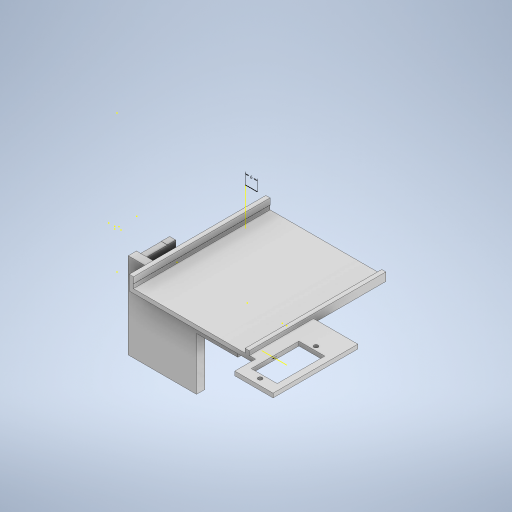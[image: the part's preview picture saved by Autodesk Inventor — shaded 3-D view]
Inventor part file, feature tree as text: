
AUTODESK INVENTOR PART (.ipt)
format: ipt  version: 2023 (Build 270158000, 158)  size: 867,840 bytes
history: native  units: mm
features: sketch x88, extrude x69, thread x4
ambient origin geometry x8: Origin, YZ Plane, XZ Plane, XY Plane, X Axis, Y Axis, Z Axis, Center Point
bodies: Solid1 (feature_tree)
feature tree (161):
  extrude  "Extrusion1"  Depth=50.0mm
  sketch  "Sketch2"  dims[d2=2.0mm d3=0.0mm d4=4.0mm]
  extrude  "Extrusion2"  Depth=4.0mm
  sketch  "Sketch4"  dims[d9=2.0mm d10=17.5mm d11=0.0mm]
  extrude  "Extrusion3"  Depth=1.0mm TaperAngle=0.0deg
  extrude  "Extrusion4"  Depth=17.5mm TaperAngle=0.0deg
  extrude  "Extrusion5"  Depth=2.0mm
  extrude  "Extrusion6"  Depth=2.0mm
  extrude  "Extrusion7"  Depth=9.0mm
  sketch  "Sketch9"  dims[d25=20.5mm d26=0.0mm d27=2.0mm]
  extrude  "Extrusion8"  Depth=2.0mm TaperAngle=0.0deg
  extrude  "Extrusion9"  Depth=2.0mm
  extrude  "Extrusion10"  Depth=10.0mm TaperAngle=0.0deg
  extrude  "Extrusion11"  Depth=10.0mm TaperAngle=0.0deg
  extrude  "Extrusion12"  Depth=2.0mm
  extrude  "Extrusion13"  Depth=2.0mm TaperAngle=0.0deg
  extrude  "Extrusion14"  Depth=15.0mm
  extrude  "Extrusion15"  Depth=5.0mm TaperAngle=0.0deg
  extrude  "Extrusion16"  Depth=2.0mm
  extrude  "Extrusion17"  Depth=2.0mm
  sketch  "Sketch20"  dims[d65=5.0mm d66=0.0mm d67=2.0mm d68=0.0mm]
  extrude  "Extrusion18"  Depth=10.0mm TaperAngle=0.0deg
  extrude  "Extrusion19"  Depth=2.0mm
  sketch  "Sketch23"  dims[d77=2.0mm d78=2.0mm d79=0.0mm]
  sketch  "Sketch24"  dims[d80=18.0mm d81=2.0mm d82=0.0mm]
  extrude  "Extrusion20"  Depth=2.0mm TaperAngle=0.0deg
  extrude  "Extrusion21"  Depth=30.0mm TaperAngle=0.0deg
  extrude  "Extrusion22"  Depth=4.0mm TaperAngle=0.0deg
  sketch  "Sketch28"  dims[d96=2.0mm d97=10.0mm d98=0.0mm]
  extrude  "Extrusion23"  Depth=2.0mm TaperAngle=0.0deg
  extrude  "Extrusion24"  Depth=2.0mm TaperAngle=0.0deg
  sketch  "Sketch31"  dims[d107=6.0mm d108=0.0mm d109=3.0mm]
  extrude  "Extrusion25"  Depth=2.0mm
  extrude  "Extrusion26"  Depth=2.0mm
  thread  "Thread1"  [1 undecoded]
  thread  "Thread2"  [1 undecoded]
  extrude  "Extrusion27"  Depth=2.0mm TaperAngle=0.0deg
  extrude  "Extrusion28"  Depth=10.0mm TaperAngle=0.0deg
  extrude  "Extrusion29"  Depth=10.0mm TaperAngle=0.0deg
  extrude  "Extrusion30"  Depth=3.0mm TaperAngle=0.0deg
  extrude  "Extrusion31"  Depth=3.0mm
  extrude  "Extrusion32"  Depth=12.0mm TaperAngle=0.0deg
  extrude  "Extrusion33"  Depth=50.0mm TaperAngle=0.0deg
  sketch  "Sketch41"  dims[d141=10.0mm d142=0.0mm d143=20.0mm d144=0.0mm]
  sketch  "Sketch42"  dims[d145=2.0mm d146=2.0mm d147=0.0mm]
  extrude  "Extrusion34"  Depth=10.0mm TaperAngle=0.0deg
  extrude  "Extrusion35"  Depth=4.0mm TaperAngle=0.0deg
  sketch  "Sketch45"  dims[d156=3.0mm d157=10.0mm d158=0.0mm]
  extrude  "Extrusion36"  Depth=4.0mm
  sketch  "Sketch47"  dims[d162=3.0mm d163=26.0mm d164=0.0mm]
  extrude  "Extrusion37"  Depth=4.0mm
  extrude  "Extrusion38"  Depth=10.0mm TaperAngle=0.0deg
  extrude  "Extrusion39"  Depth=20.0mm TaperAngle=0.0deg
  extrude  "Extrusion40"  Depth=10.0mm TaperAngle=0.0deg
  extrude  "Extrusion41"  Depth=20.0mm TaperAngle=0.0deg
  sketch  "Sketch52"  dims[d178=10.0mm d179=0.0mm]
  extrude  "Extrusion42"  Depth=2.0mm TaperAngle=0.0deg
  sketch  "Sketch54"
  extrude  "Extrusion43"  Depth=3.0mm TaperAngle=0.0deg
  extrude  "Extrusion44"  Depth=5.0mm TaperAngle=0.0deg
  sketch  "Sketch57"
  sketch  "Sketch58"
  sketch  "Sketch59"
  extrude  "Extrusion45"  Depth=10.0mm TaperAngle=0.0deg
  extrude  "Extrusion46"  Depth=15.5mm TaperAngle=0.0deg
  sketch  "Sketch61"
  extrude  "Extrusion47"  Depth=3.0mm TaperAngle=0.0deg
  extrude  "Extrusion48"  Depth=3.0mm TaperAngle=0.0deg
  extrude  "Extrusion49"  Depth=2.0mm
  sketch  "Sketch65"
  extrude  "Extrusion50"  Depth=10.0mm TaperAngle=0.0deg
  extrude  "Extrusion51"  Depth=2.0mm TaperAngle=0.0deg
  extrude  "Extrusion52"  [1 undecoded]
  extrude  "Extrusion53"  [1 undecoded]
  extrude  "Extrusion54"  [1 undecoded]
  extrude  "Extrusion55"  [1 undecoded]
  extrude  "Extrusion56"  [1 undecoded]
  sketch  "Sketch73"
  extrude  "Extrusion57"  [1 undecoded]
  extrude  "Extrusion58"  [1 undecoded]
  sketch  "Sketch76"
  extrude  "Extrusion59"  [1 undecoded]
  extrude  "Extrusion60"  [1 undecoded]
  extrude  "Extrusion61"  [1 undecoded]
  extrude  "Extrusion62"  [1 undecoded]
  sketch  "Sketch81"
  extrude  "Extrusion63"  [1 undecoded]
  extrude  "Extrusion64"  [1 undecoded]
  extrude  "Extrusion65"  [1 undecoded]
  extrude  "Extrusion66"  [1 undecoded]
  extrude  "Extrusion67"  [1 undecoded]
  extrude  "Extrusion68"  [1 undecoded]
  thread  "Thread3"  [1 undecoded]
  thread  "Thread4"  [1 undecoded]
  extrude  "Extrusion69"  [1 undecoded]
  sketch  "Sketch1"  dims[d0=23.0mm d1=50.0mm]
  sketch  "Sketch3"  dims[d5=1.0mm d6=0.0mm d7=29.0mm d8=0.0mm]
  sketch  "Sketch5"  dims[d12=17.5mm d13=0.0mm d14=2.0mm]
  sketch  "Sketch6"  dims[d15=32.0mm d16=0.0mm d17=2.0mm]
  sketch  "Sketch7"  dims[d18=32.0mm d19=0.0mm d20=9.0mm]
  sketch  "Sketch8"  dims[d21=50.0mm d22=0.0mm d23=2.0mm d24=0.0mm]
  sketch  "Sketch10"  dims[d28=20.5mm d29=0.0mm d30=10.0mm d31=0.0mm]
  sketch  "Sketch11"  dims[d32=10.0mm d33=0.0mm d34=10.0mm d35=0.0mm]
  sketch  "Sketch12"  dims[d36=10.0mm d37=0.0mm d38=2.0mm]
  sketch  "Sketch13"  dims[d39=13.0mm d40=0.0mm d41=2.0mm d42=0.0mm]
  sketch  "Sketch14"  dims[d43=2.0mm d44=0.0mm d45=15.0mm]
  sketch  "Sketch15"  dims[d46=4.0mm d47=0.0mm d48=5.0mm d49=0.0mm]
  sketch  "Sketch16"  dims[d50=14.0mm d51=0.0mm d52=2.0mm]
  sketch  "Sketch17"  dims[d53=25.0mm d54=0.0mm d55=2.0mm]
  sketch  "Sketch18"  dims[d56=25.0mm d57=0.0mm d58=10.0mm d59=0.0mm]
  sketch  "Sketch19"  dims[d60=2.0mm d61=0.0mm d63=2.0mm]
  sketch  "Sketch21"  dims[d69=2.0mm d70=0.0mm d71=30.0mm d72=0.0mm]
  sketch  "Sketch22"  dims[d73=2.0mm d74=0.0mm d75=4.0mm d76=0.0mm]
  sketch  "Sketch25"  dims[d83=2.0mm d84=0.0mm d85=0.389mm]
  sketch  "Sketch26"  dims[d86=2.0mm d87=0.0mm d88=6.0mm d89=6.0mm d90=0.0mm d91=6.0mm d92=0.0mm]
  sketch  "Sketch27"  dims[d93=2.0mm d94=6.0mm d95=0.0mm]
  sketch  "Sketch29"  dims[d99=10.0mm d100=0.0mm d101=10.0mm d102=0.0mm]
  sketch  "Sketch30"  dims[d103=10.0mm d104=0.0mm d105=3.0mm d106=0.0mm]
  sketch  "Sketch32"  dims[d110=3.0mm d111=12.0mm d112=0.0mm]
  sketch  "Sketch33"  dims[d113=60.0mm d114=0.0mm d115=50.0mm d116=0.0mm]
  sketch  "Sketch34"  dims[d117=50.0mm d118=0.0mm d119=10.0mm d120=0.0mm]
  sketch  "Sketch35"  dims[d121=2.0mm d122=0.0mm d123=4.0mm d124=0.0mm]
  sketch  "Sketch36"  dims[d125=8.0mm d126=4.0mm]
  sketch  "Sketch37"  dims[d127=4.0mm d128=4.0mm]
  sketch  "Sketch38"  dims[d129=4.0mm d130=0.0mm d131=10.0mm d132=0.0mm]
  sketch  "Sketch39"  dims[d133=20.0mm d134=0.0mm d135=20.0mm d136=0.0mm]
  sketch  "Sketch40"  dims[d137=20.0mm d138=0.0mm d139=10.0mm d140=0.0mm]
  sketch  "Sketch43"  dims[d148=2.0mm d149=0.0mm d150=3.0mm d151=0.0mm]
  sketch  "Sketch44"  dims[d152=3.0mm d153=0.0mm d154=5.0mm d155=0.0mm]
  sketch  "Sketch46"  dims[d159=5.0mm d160=15.5mm d161=0.0mm]
  sketch  "Sketch48"  dims[d165=3.0mm d166=26.0mm d167=0.0mm]
  sketch  "Sketch49"  dims[d168=10.0mm d169=0.0mm d170=2.0mm]
  sketch  "Sketch50"  dims[d171=2.0mm d172=10.0mm d173=0.0mm]
  sketch  "Sketch51"  dims[d174=2.0mm d175=0.0mm d176=2.0mm d177=0.0mm]
  sketch  "Sketch53"
  sketch  "Sketch55"
  sketch  "Sketch56"
  sketch  "Sketch60"
  sketch  "Sketch62"
  sketch  "Sketch63"
  sketch  "Sketch64"
  sketch  "Sketch66"
  sketch  "Sketch67"
  sketch  "Sketch68"
  sketch  "Sketch69"
  sketch  "Sketch70"
  sketch  "Sketch71"
  sketch  "Sketch72"
  sketch  "Sketch74"
  sketch  "Sketch75"
  sketch  "Sketch77"
  sketch  "Sketch78"
  sketch  "Sketch79"
  sketch  "Sketch80"
  sketch  "Sketch82"
  sketch  "Sketch83"
  sketch  "Sketch84"
  sketch  "Sketch85"
  sketch  "Sketch86"
  sketch  "Sketch87"
  sketch  "Sketch88"
note: 22 required parameter values undecoded (feature->parameter linkage not recoverable at this tier; creation-order binding heuristic only, values carry confidence <= 0.55)
